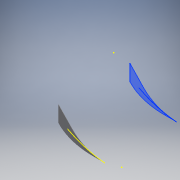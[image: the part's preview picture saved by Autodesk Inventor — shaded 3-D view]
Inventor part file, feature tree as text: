
AUTODESK INVENTOR PART (.ipt)
format: ipt  version: 2018 (Build 220112000, 112)  size: 157,184 bytes
history: native  units: mm
features: extrude x3, sketch x3, shell x1
ambient origin geometry x8: Origin, YZ Plane, XZ Plane, XY Plane, X Axis, Y Axis, Z Axis, Center Point
bodies: Body1 (feature_tree)
feature tree (7):
  extrude  "押し出し1"  Depth=350.0mm
  extrude  "押し出し2"  Depth=603.642mm
  shell  "シェル1"  Thickness=70.0mm
  extrude  "押し出し3"  Depth=10.0mm TaperAngle=0.0deg
  sketch  "スケッチ1"
  sketch  "スケッチ2"
  sketch  "スケッチ5"
